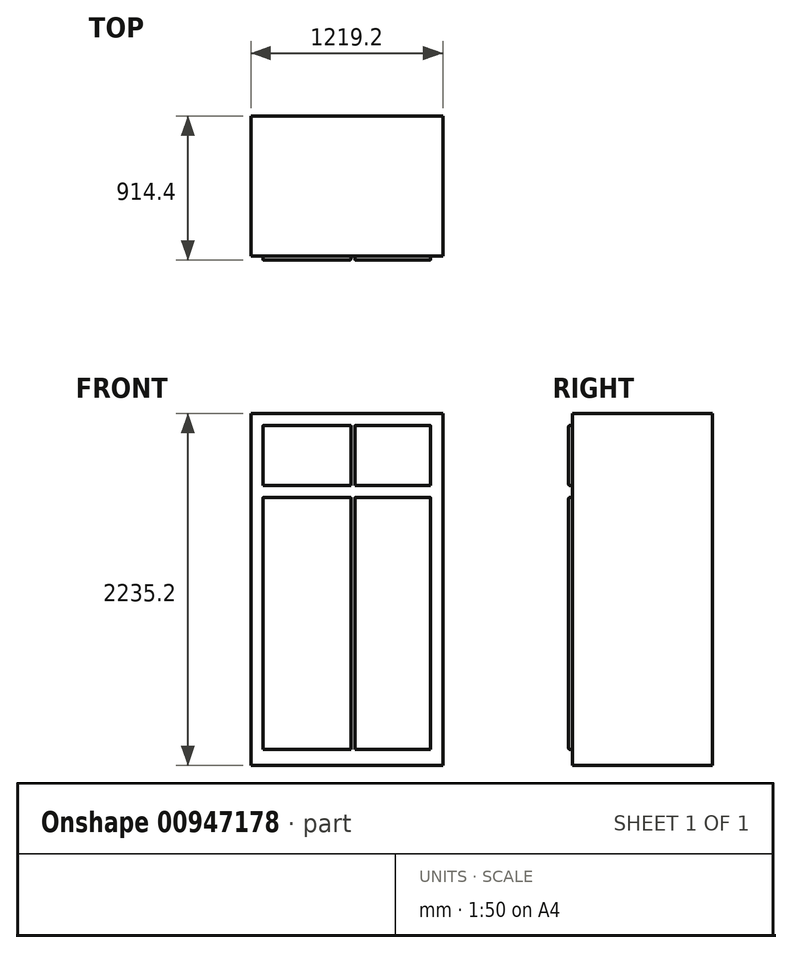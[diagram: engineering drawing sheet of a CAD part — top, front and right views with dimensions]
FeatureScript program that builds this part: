
annotation { "Feature Type Name" : "Feature", "Feature Type Description" : "" }
export const myFeature = defineFeature(function(context is Context, id is Id, definition is map)
    precondition{}
    {
        {
            var Q0;
            Q0=qCreatedBy(makeId("Top.planeOp"),FACE);
            var sketch = newSketch(context, id + "F0", { "sketchPlane" : qUnion([Q0])});
            skLineSegment(sketch, "E0.bottom", {"start": v(-157.48, 0) * mm, "end": v(1061.72, 0) * mm});
            skLineSegment(sketch, "E0.top", {"start": v(-157.48, 889) * mm, "end": v(1061.72, 889) * mm});
            skLineSegment(sketch, "E0.left", {"start": v(-157.48, 0) * mm, "end": v(-157.48, 889) * mm});
            skLineSegment(sketch, "E0.right", {"start": v(1061.72, 0) * mm, "end": v(1061.72, 889) * mm});
            skSolve(sketch);
        }
        {
            var Q0;
            Q0 = qSketchRegion(id + "F0", true);
            extrude(context, id + "F1", {"entities" : qUnion([Q0]), "depth" : 2235.2 * mm, "offsetDistance" : 25.4 * mm});
        }
        {
            var Q0;
            Q0=makeQuery(id+"F1.opExtrude","SWEPT_FACE",FACE,{"disambiguationData":[OSD([sQuery(id+"F0.wireOp",EDGE,"E0.bottom")])]});
            var sketch = newSketch(context, id + "F2", { "sketchPlane" : qUnion([Q0])});
            skLineSegment(sketch, "E1.bottom", {"start": v(-81.28, 1701.8) * mm, "end": v(477.52, 1701.8) * mm});
            skLineSegment(sketch, "E1.top", {"start": v(-81.28, 101.6) * mm, "end": v(477.52, 101.6) * mm});
            skLineSegment(sketch, "E1.left", {"start": v(-81.28, 1701.8) * mm, "end": v(-81.28, 101.6) * mm});
            skLineSegment(sketch, "E1.right", {"start": v(477.52, 1701.8) * mm, "end": v(477.52, 101.6) * mm});
            skLineSegment(sketch, "E2.bottom", {"start": v(502.92, 1701.8) * mm, "end": v(985.52, 1701.8) * mm});
            skLineSegment(sketch, "E2.top", {"start": v(502.92, 101.6) * mm, "end": v(985.52, 101.6) * mm});
            skLineSegment(sketch, "E2.left", {"start": v(502.92, 1701.8) * mm, "end": v(502.92, 101.6) * mm});
            skLineSegment(sketch, "E2.right", {"start": v(985.52, 1701.8) * mm, "end": v(985.52, 101.6) * mm});
            skLineSegment(sketch, "E3.bottom", {"start": v(-81.28, 2159) * mm, "end": v(477.52, 2159) * mm});
            skLineSegment(sketch, "E3.top", {"start": v(-81.28, 1778) * mm, "end": v(477.52, 1778) * mm});
            skLineSegment(sketch, "E3.left", {"start": v(-81.28, 2159) * mm, "end": v(-81.28, 1778) * mm});
            skLineSegment(sketch, "E3.right", {"start": v(477.52, 2159) * mm, "end": v(477.52, 1778) * mm});
            skLineSegment(sketch, "E4.bottom", {"start": v(502.92, 2159) * mm, "end": v(985.52, 2159) * mm});
            skLineSegment(sketch, "E4.top", {"start": v(502.92, 1778) * mm, "end": v(985.52, 1778) * mm});
            skLineSegment(sketch, "E4.left", {"start": v(502.92, 2159) * mm, "end": v(502.92, 1778) * mm});
            skLineSegment(sketch, "E4.right", {"start": v(985.52, 2159) * mm, "end": v(985.52, 1778) * mm});
            skSolve(sketch);
        }
        {
            var Q0;
            Q0 = qSketchRegion(id + "F2", true);
            extrude(context, id + "F3", {"entities" : qUnion([Q0]), "operationType" : NewBodyOperationType.ADD, "depth" : 25.4 * mm, "offsetDistance" : 25.4 * mm});
        }
        {
            var Q0;
            Q0=makeQuery(id+"F3.opExtrude","CAP_FACE",FACE,{"disambiguationData":[OSD([sQuery(id+"F2.wireOp",EDGE,"E4.bottom"),sQuery(id+"F2.wireOp",EDGE,"E4.top"),sQuery(id+"F2.wireOp",EDGE,"E4.left"),sQuery(id+"F2.wireOp",EDGE,"E4.right")])],"isStart":false});
            var Q1;
            Q1=makeQuery(id+"F3.opExtrude","CAP_FACE",FACE,{"disambiguationData":[OSD([sQuery(id+"F2.wireOp",EDGE,"E3.bottom"),sQuery(id+"F2.wireOp",EDGE,"E3.top"),sQuery(id+"F2.wireOp",EDGE,"E3.left"),sQuery(id+"F2.wireOp",EDGE,"E3.right")])],"isStart":false});
            var Q2;
            Q2=makeQuery(id+"F3.opExtrude","CAP_FACE",FACE,{"disambiguationData":[OSD([sQuery(id+"F2.wireOp",EDGE,"E1.bottom"),sQuery(id+"F2.wireOp",EDGE,"E1.top"),sQuery(id+"F2.wireOp",EDGE,"E1.left"),sQuery(id+"F2.wireOp",EDGE,"E1.right")])],"isStart":false});
            var Q3;
            Q3=makeQuery(id+"F3.opExtrude","CAP_FACE",FACE,{"disambiguationData":[OSD([sQuery(id+"F2.wireOp",EDGE,"E2.bottom"),sQuery(id+"F2.wireOp",EDGE,"E2.top"),sQuery(id+"F2.wireOp",EDGE,"E2.left"),sQuery(id+"F2.wireOp",EDGE,"E2.right")])],"isStart":false});
            fillet(context, id + "F4", {"entities" : qUnion([Q0, Q1, Q2, Q3]), "radius" : 6.35 * mm, "tangentPropagation" : true, "allowEdgeOverflow" : false});
        }
    });
